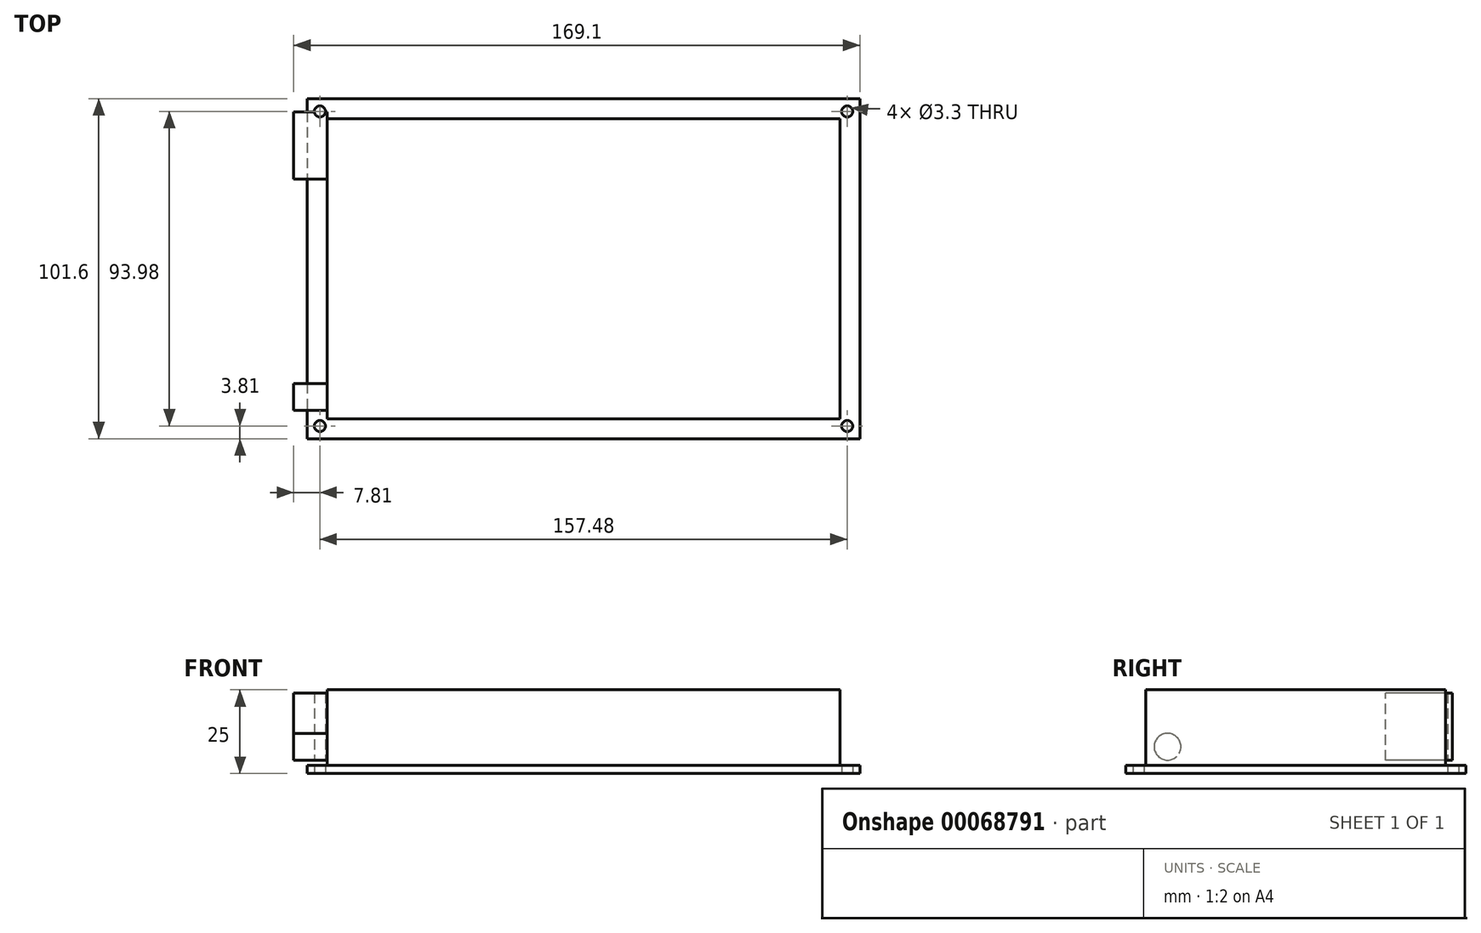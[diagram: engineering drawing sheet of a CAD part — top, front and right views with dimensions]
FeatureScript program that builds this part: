
annotation { "Feature Type Name" : "Feature", "Feature Type Description" : "" }
export const myFeature = defineFeature(function(context is Context, id is Id, definition is map)
    precondition{}
    {
        {
            var Q0;
            Q0=qCreatedBy(makeId("Top.planeOp"),FACE);
            var sketch = newSketch(context, id + "F0", { "sketchPlane" : qUnion([Q0])});
            skLineSegment(sketch, "E0.bottom", {"start": v(0, 0) * mm, "end": v(165.1, 0) * mm});
            skLineSegment(sketch, "E0.top", {"start": v(0, -101.6) * mm, "end": v(165.1, -101.6) * mm});
            skLineSegment(sketch, "E0.left", {"start": v(0, 0) * mm, "end": v(0, -101.6) * mm});
            skLineSegment(sketch, "E0.right", {"start": v(165.1, 0) * mm, "end": v(165.1, -101.6) * mm});
            skPoint(sketch, "E1", {"position": v(3.81, -97.8) * mm});
            skLineSegment(sketch, "E2", {"start": v(0, -50.8) * mm, "end": v(165.1, -50.8) * mm, "construction": true});
            skLineSegment(sketch, "E3", {"start": v(82.55, 0) * mm, "end": v(82.55, -101.6) * mm, "construction": true});
            skPoint(sketch, "E4.MirrorP", {"position": v(161.3, -97.8) * mm});
            skPoint(sketch, "E5.MirrorP", {"position": v(3.81, -3.8) * mm});
            skPoint(sketch, "E6.MirrorP", {"position": v(161.3, -3.8) * mm});
            skPoint(sketch, "E7", {"position": v(0, -91.19) * mm});
            skPoint(sketch, "E8", {"position": v(0, -87) * mm});
            skLineSegment(sketch, "E9", {"start": v(0, -91.19) * mm, "end": v(0, -87) * mm});
            skPoint(sketch, "E10", {"position": v(0, -89.1) * mm});
            skPoint(sketch, "E11", {"position": v(0, -20.32) * mm});
            skPoint(sketch, "E12", {"position": v(0, -7.62) * mm});
            skLineSegment(sketch, "E13", {"start": v(0, -7.62) * mm, "end": v(0, -20.32) * mm});
            skPoint(sketch, "E14", {"position": v(0, -13.97) * mm});
            skLineSegment(sketch, "E15.0", {"start": v(6, -6) * mm, "end": v(6, -95.6) * mm});
            skLineSegment(sketch, "E15.1", {"start": v(6, -6) * mm, "end": v(159.1, -6) * mm});
            skLineSegment(sketch, "E15.2", {"start": v(159.1, -6) * mm, "end": v(159.1, -95.6) * mm});
            skLineSegment(sketch, "E15.3", {"start": v(6, -95.6) * mm, "end": v(159.1, -95.6) * mm});
            skSolve(sketch);
        }
        {
            var Q0;
            {var subQ3=sQuery(id+"F0.wireOp",EDGE,"E0.bottom");Q0=makeQuery(id+"F0.imprint","IMPRINT",FACE,{"disambiguationData":[TD([[makeQuery(id+"F0.imprint","IMPRINT",EDGE,{"derivedFrom":subQ3}),-1.0]])]});}
            extrude(context, id + "F1", {"entities" : qUnion([Q0]), "depth" : 2.4 * mm});
        }
        {
            var Q0;
            Q0=makeQuery(id+"F0.imprint","IMPRINT",FACE,{"disambiguationData":[TD([[makeQuery(id+"F0.imprint","IMPRINT",EDGE,{"derivedFrom":sQuery(id+"F0.wireOp",EDGE,"E15.0")}),1.0]])]});
            extrude(context, id + "F2", {"entities" : qUnion([Q0]), "operationType" : NewBodyOperationType.ADD, "depth" : 25 * mm});
        }
        {
            var Q0;
            Q0=makeQuery(id+"F1.opExtrude","SWEPT_FACE",FACE,{"disambiguationData":[OSD([sQuery(id+"F0.wireOp",EDGE,"E0.left"),sQuery(id+"F0.wireOp",EDGE,"E9"),sQuery(id+"F0.wireOp",EDGE,"E13")])]});
            var sketch = newSketch(context, id + "F3", { "sketchPlane" : qUnion([Q0])});
            skPoint(sketch, "E16.0", {"position": v(89.1, 0) * mm});
            skPoint(sketch, "E16.1", {"position": v(13.97, 0) * mm});
            skPoint(sketch, "E17", {"position": v(13.97, 14) * mm});
            skPoint(sketch, "E18", {"position": v(89.1, 8) * mm});
            skLineSegment(sketch, "E19.bottom", {"start": v(3.97, 4) * mm, "end": v(23.97, 4) * mm});
            skLineSegment(sketch, "E19.top", {"start": v(3.97, 24) * mm, "end": v(23.97, 24) * mm});
            skLineSegment(sketch, "E19.left", {"start": v(3.97, 4) * mm, "end": v(3.97, 24) * mm});
            skLineSegment(sketch, "E19.right", {"start": v(23.97, 4) * mm, "end": v(23.97, 24) * mm});
            skCircle(sketch, "E20", {"center": v(89.1, 8) * mm, "radius": 4 * mm});
            skSolve(sketch);
        }
        {
            var Q0;
            Q0=makeQuery(id+"F3.imprint","IMPRINT",FACE,{"disambiguationData":[TD([[makeQuery(id+"F3.imprint","IMPRINT",EDGE,{"derivedFrom":sQuery(id+"F3.wireOp",EDGE,"E19.bottom")}),1.0]])]});
            var Q1;
            Q1=makeQuery(id+"F3.imprint","IMPRINT",FACE,{"disambiguationData":[TD([[makeQuery(id+"F3.imprint","IMPRINT",EDGE,{"derivedFrom":sQuery(id+"F3.wireOp",EDGE,"E20")}),1.0]])]});
            var Q2;
            Q2=makeQuery(id+"F2.opExtrude","SWEPT_FACE",FACE,{"disambiguationData":[OSD([sQuery(id+"F0.wireOp",EDGE,"E15.0")])]});
            extrude(context, id + "F4", {"entities" : qUnion([Q0, Q1]), "operationType" : NewBodyOperationType.ADD, "endBound" : BoundingType.UP_TO_SURFACE, "oppositeDirection" : true, "endBoundEntityFace" : qUnion([Q2]), "depth" : 4 * mm, "hasSecondDirection" : true, "secondDirectionOppositeDirection" : false, "secondDirectionDepth" : 4 * mm});
        }
        {
            var Q0;
            Q0=sQuery(id+"F0.wireOp",VERTEX,"E5.MirrorP");
            var Q1;
            Q1=sQuery(id+"F0.wireOp",VERTEX,"E1");
            var Q2;
            Q2=sQuery(id+"F0.wireOp",VERTEX,"E4.MirrorP");
            var Q3;
            Q3=sQuery(id+"F0.wireOp",VERTEX,"E6.MirrorP");
            var Q4;
            Q4=makeQuery(id+"F1.opExtrude","SWEPT_BODY",BODY,{"disambiguationData":[OSD([sQuery(id+"F0.wireOp",EDGE,"E0.bottom"),sQuery(id+"F0.wireOp",EDGE,"E0.top"),sQuery(id+"F0.wireOp",EDGE,"E0.left"),sQuery(id+"F0.wireOp",EDGE,"E0.right"),sQuery(id+"F0.wireOp",EDGE,"E9"),sQuery(id+"F0.wireOp",EDGE,"E13"),sQuery(id+"F0.wireOp",EDGE,"E15.0"),sQuery(id+"F0.wireOp",EDGE,"E15.1"),sQuery(id+"F0.wireOp",EDGE,"E15.2"),sQuery(id+"F0.wireOp",EDGE,"E15.3")])]});
            hole(context, id + "F5", {"style" : HoleStyle.SIMPLE, "endStyle" : HoleEndStyle.THROUGH, "oppositeDirection" : true, "standardTappedOrClearance" : lookupTablePath({ "standard" : "ISO", "fit" : "Normal", "size" : "M3", "type" : "Clearance" }), "standardBlindInLast" : lookupTablePath({ "fit" : "Standard", "standard" : "ISO", "size" : "M3", "type" : "Clearance" }), "holeDiameter" : 3.3 * mm, "locations" : qUnion([Q0, Q1, Q2, Q3]), "scope" : qUnion([Q4]), "isTappedThrough" : true});
        }
    });
